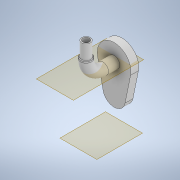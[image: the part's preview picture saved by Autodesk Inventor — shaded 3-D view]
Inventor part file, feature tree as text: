
AUTODESK INVENTOR PART (.ipt)
format: ipt  version: 2020 (Build 240168000, 168)  size: 180,736 bytes
history: native  units: in
note: dims shown in document units (in); Inventor stores cm internally (conversion verified against a paired STEP export)
features: sketch x4, extrude x3, plane x1, hole x1, other x1
ambient origin geometry x8: Origin, YZ Plane, XZ Plane, XY Plane, X Axis, Y Axis, Z Axis, Center Point
bodies: Body1 (feature_tree)
feature tree (10):
  extrude  "Extrusion8"  Depth=1.1811in
  extrude  "Extrusion9"  Depth=0.3937in
  plane  "Work Plane8"
  hole  "Hole1"  [1 undecoded]
  extrude  "Extrusion11"  Depth=0.5118in TaperAngle=0.0deg
  other  "Bend Part3"
  sketch  "Sketch8"  dims[d32=0.7874in d33=1.1811in]
  sketch  "Sketch13"  dims[d34=0.2756in d35=0.0in d36=0.3937in]
  sketch  "Sketch14"  dims[d37=1.5748in d38=0.0in]
  sketch  "Sketch15"  dims[d45=0.2362in d46=0.2362in d47=0.315in d48=0.2756in d49=90.0deg d50=0.315in d51=0.8108in d52=0.315in d53=0.5118in d54=0.0in d55=1.1811in d56=0.3937in d57=90.0deg d31=0.0197in]
note: 1 required parameter value undecoded (feature->parameter linkage not recoverable at this tier; creation-order binding heuristic only, values carry confidence <= 0.55)
